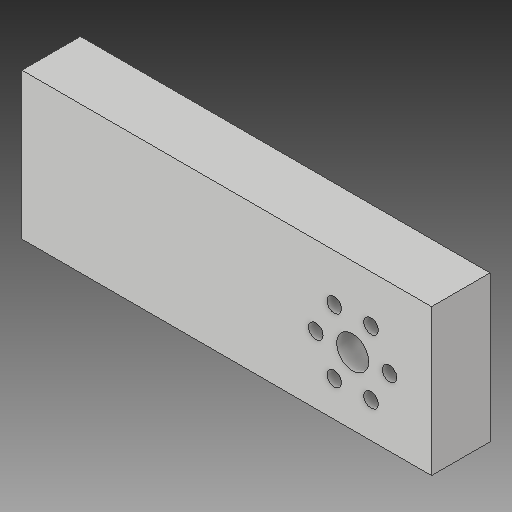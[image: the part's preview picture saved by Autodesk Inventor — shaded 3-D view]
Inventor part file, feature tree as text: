
AUTODESK INVENTOR PART (.ipt)
format: ipt  version: 2019 (Build 230136000, 136)  size: 139,264 bytes
history: native  units: in
note: dims shown in document units (in); Inventor stores cm internally (conversion verified against a paired STEP export)
features: thicken_offset x3, sketch x3, extrude x2, hole x1
ambient origin geometry x8: Origin, YZ Plane, XZ Plane, XY Plane, X Axis, Y Axis, Z Axis, Center Point
bodies: Solid1 (feature_tree)
feature tree (9):
  extrude  "Extrusion1"  Depth=1.25in
  extrude  "Extrusion2"  Depth=0.575in
  thicken_offset  "Thicken1"
  thicken_offset  "Thicken2"
  thicken_offset  "Thicken3"
  hole  "Hole1"  [1 undecoded]
  sketch  "Sketch1"  dims[d0=2.5in d1=1.25in]
  sketch  "Sketch2"  dims[d2=0.75in d3=0.0in d6=0.575in]
  sketch  "Sketch5"  dims[d7=0.275in d9=0.63in d15=0.75in d16=0.0in d17=0.125in d18=2.3622in d20=360.0deg d35=1.0in d36=1.0in d37=0.125in d38=0.125in d41=0.125in d42=0.125in d50=0.13in d51=0.25in d52=0.375in d53=0.25in d54=0.5635in d55=0.3in d56=0.8108in d57=0.25in d58=1.75in d59=3.5in d60=0.25in d61=0.674in]
note: 1 required parameter value undecoded (feature->parameter linkage not recoverable at this tier; creation-order binding heuristic only, values carry confidence <= 0.55)
